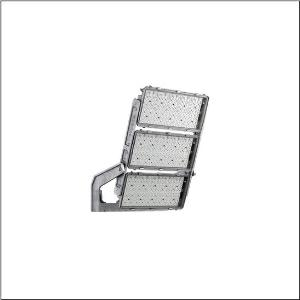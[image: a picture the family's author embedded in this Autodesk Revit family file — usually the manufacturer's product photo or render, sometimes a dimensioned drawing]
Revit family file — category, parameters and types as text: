
# Revit family: floodlight_fl_11_maxi_pro_remote___pl64blc_5xa779427w01aa_301c
name_source: partatom
category: Lighting Fixtures
units: mm (PartAtom-declared; Revit-internal decimal feet)

## family parameters
Cut with Voids When Loaded = No
Host = Face
Light Source = No
Part Type = Normal
Room Calculation Point = No
Round Connector Dimension = Use Diameter
Shared = No

## types (1)
- --- (1 x LED, 142820 lm, 1517.1 W, 5000K)
    Apparent Load = 1517 VA
    CIE Flux Codes = 28 83 99 100 100
    Color Rendering = 70
    Color Temperature = 5000K
    Default Elevation = 1800 mm
    Description = Floodlight FL 11  maxi  pro Remote floodlight; light control with lens of PMMA; cover panel of toughened safety glass, transparent; light distribution: PL64BLC, asymmetric direct distribution, LEDcolour temperature: 5000K, rated luminous flux: 142.820lm, colour rendering: CRI > 70, light colour: 750; luminous efficacy: 94lm/W; brightness control: DALI 2 (1 DALI address); with terminal, 8-pole, max. 2.5mm², mains connection: 220..240V/380..400V AC, 50/60Hz, surge voltage resistance: line to ground: 10kV, ECG replaceable separately, no afterglow with DALI off / DMX off command, LED unit replaceable without ESD environment, dustproof LED module, dimming range 10..100%; 1517W floodlight with 2x LED unit of diecast aluminium, coated grey; length: 713mm / width: 651mm / height: 338mm; mounting bracket, of diecast aluminium, uncoated, natural, equipment: Power, protection rating (complete): IP66; insulation class (complete): insulation class I (protective earthing); certification: CE, ENEC, VDE; ball protection: ball impact resistance with accessories, impact resistance: IK07; only for outdoor installations, rated ambient temperature 10°C, permissible operating ambient temperature: -40..+30°C, permissible storage temperature: -40..+85°C; packaging unit: 1 piece

Light Distribution: PL64BLC
    Height = 320 mm
    Lamp = 1 x LED
    Lamp Light Flux = 142820 lm
    Lamp Power = 1517.1 W
    Lamp count = 1
    Length = 1002 mm
    Luminous efficacy = 94 lm/W
    Manufacturer = Siteco
    ModVariant = No
    Model = 5XA779427W01AA
    Mounting Place = Ceiling
    Mounting Type = Surface mounted
    Number of Poles = 1
    OnlyDefault = Yes
    Power Factor = 1
    Product Name = Floodlight FL 11 maxi pro Remote | PL64BLC
    Product group = floodlight | ceiling mounted
    ProductGroupID = 303
    Protection Class = Protection class I
    Protection Degree = IP 66
    RLX_Detail_Level = 1
    RLX_Emergency_Light_Flux = 0 lm
    RLX_Emergency_Type = 0
    RLX_Emergency_Type_DB = No
    RlxData = <blob elided: 52237 chars, md5=5eeba396>
    Socket = socket
    Standby Power = 0 W
    System Light Flux = 142820 lm
    System Power = 1517 W
    Type Comments = factory setting: luminous flux: 100 % | dim-lin: 254 | 1070 mA
    Type Image = l_1006784.jpg
    URL = http://relux.com
    VarID = @adj_033213
    Voltage = 0 V
    Weight = 0.00 kg
    Width = 655 mm

## geometry (parser evidence)
native form markers: Blend x4, Sweep x14
no freeform markers — native parametric forms only
